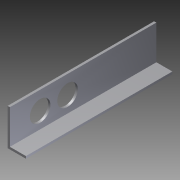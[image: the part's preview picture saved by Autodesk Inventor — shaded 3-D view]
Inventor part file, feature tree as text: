
AUTODESK INVENTOR PART (.ipt)
format: ipt  version: 2012 (Build 160160000, 160)  size: 90,624 bytes
history: native  units: in
note: dims shown in document units (in); Inventor stores cm internally (conversion verified against a paired STEP export)
features: extrude x2, sketch x2
ambient origin geometry x8: Origin, YZ Plane, XZ Plane, XY Plane, X Axis, Y Axis, Z Axis, Center Point
bodies: Solid1 (feature_tree)
feature tree (4):
  extrude  "Extrusion1"  Depth=1.0in
  extrude  "Extrusion2"  Depth=0.125in
  sketch  "Sketch1"  dims[d0=2.0in d1=1.0in]
  sketch  "Sketch2"  dims[d2=0.125in d3=0.125in d4=8.0in d5=0.0in d6=1.125in d7=1.125in d8=1.0in d9=1.65in d10=1.5in d11=8.0in d12=0.0in]
